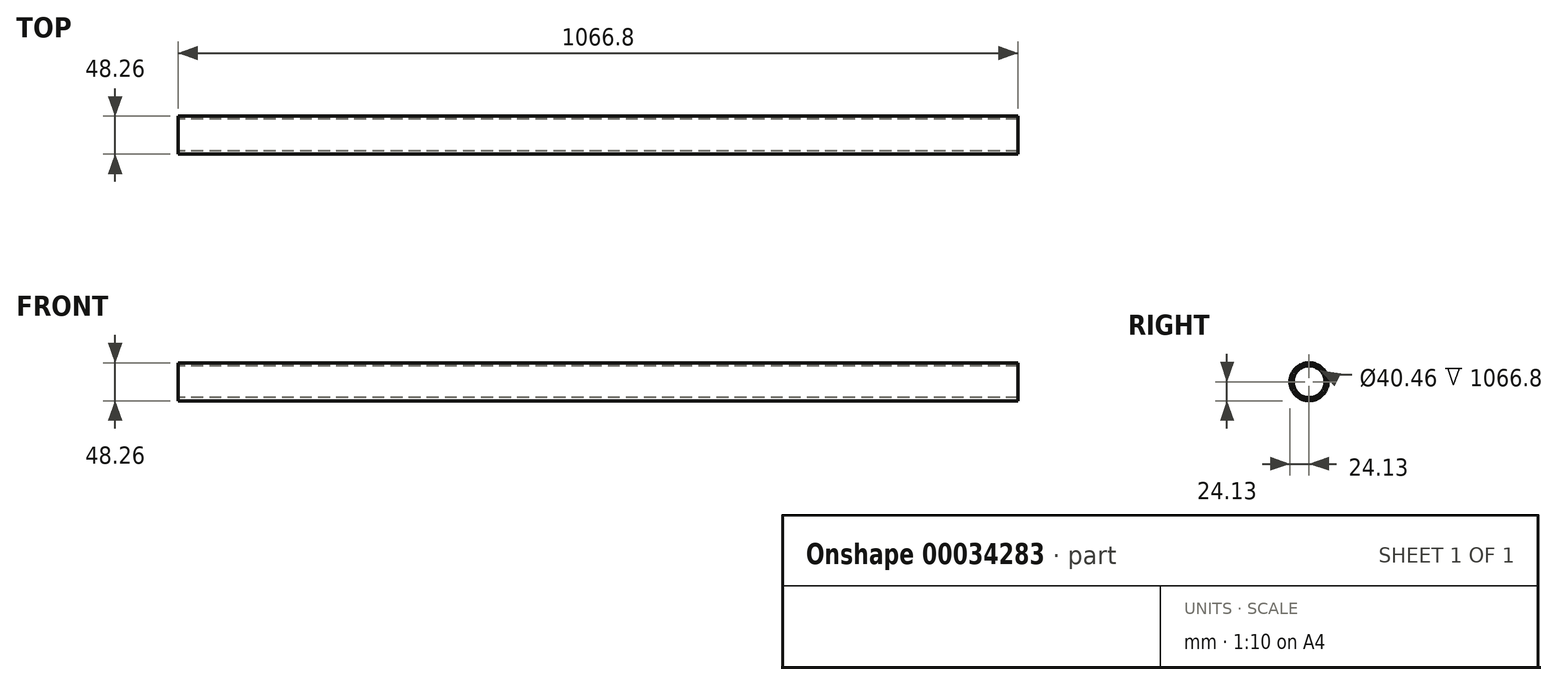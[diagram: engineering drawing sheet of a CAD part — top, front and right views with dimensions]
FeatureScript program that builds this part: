
annotation { "Feature Type Name" : "Feature", "Feature Type Description" : "" }
export const myFeature = defineFeature(function(context is Context, id is Id, definition is map)
    precondition{}
    {
        {
            var Q0;
            Q0=qCreatedBy(makeId("Right.planeOp"),FACE);
            var sketch = newSketch(context, id + "F0", { "sketchPlane" : qUnion([Q0])});
            skCircle(sketch, "E0", {"center": v(0, 0) * mm, "radius": 24.13 * mm});
            skCircle(sketch, "E1", {"center": v(0, 0) * mm, "radius": 20.23 * mm});
            skSolve(sketch);
        }
        {
            var Q0;
            Q0=makeQuery(id+"F0.imprint","IMPRINT",FACE,{"disambiguationData":[TD([[makeQuery(id+"F0.imprint","IMPRINT",EDGE,{"derivedFrom":sQuery(id+"F0.wireOp",EDGE,"E0")}),1.0]])]});
            extrude(context, id + "F1", {"entities" : qUnion([Q0]), "depth" : 1066.8 * mm});
        }
    });
